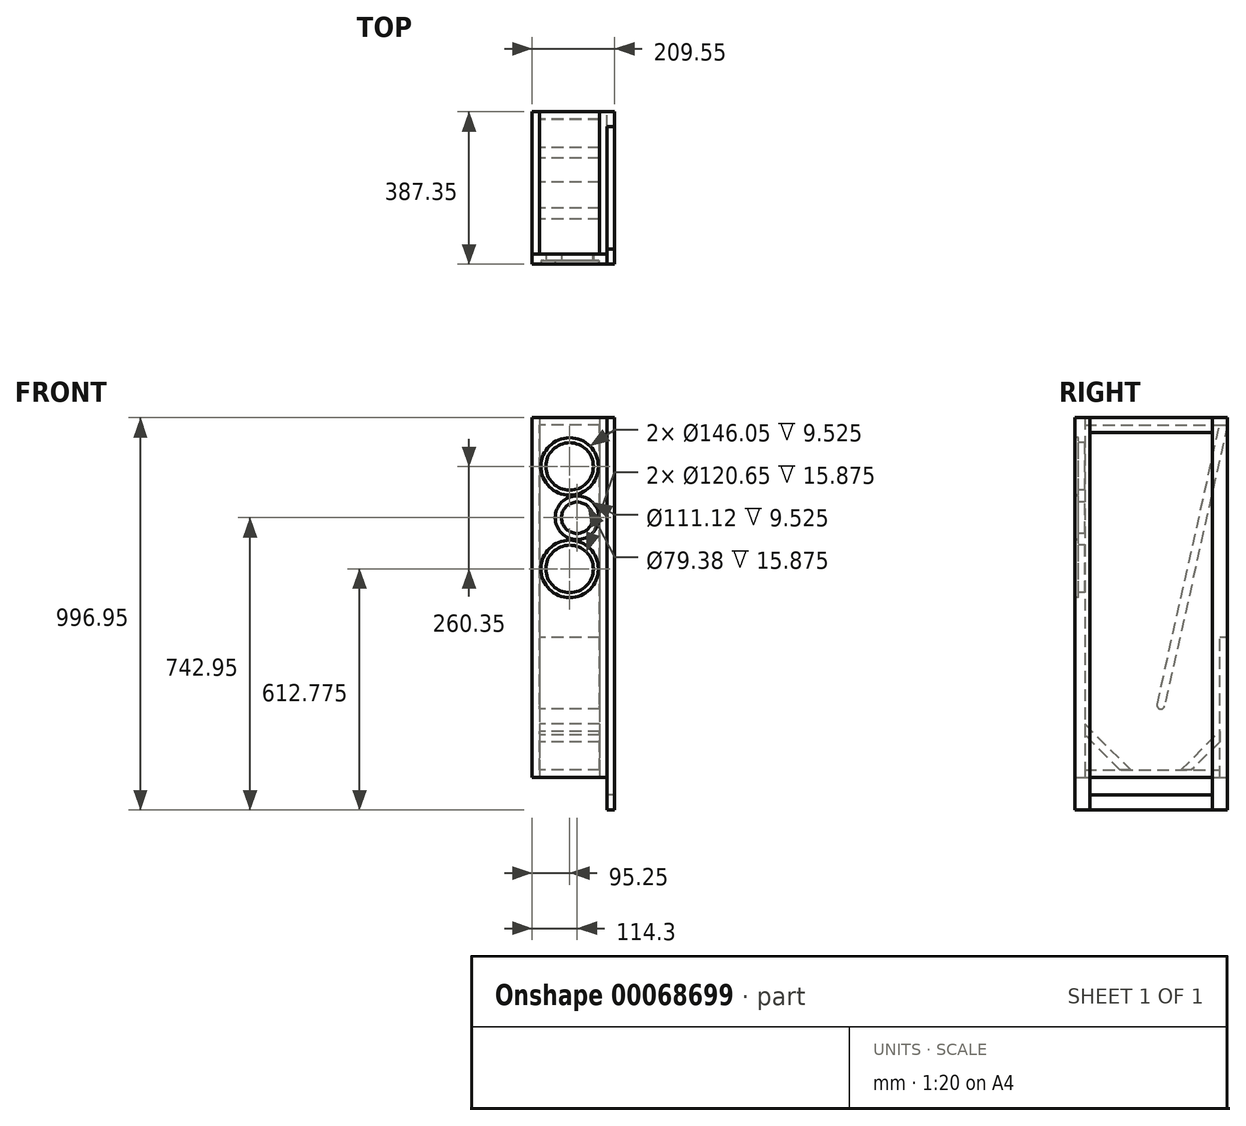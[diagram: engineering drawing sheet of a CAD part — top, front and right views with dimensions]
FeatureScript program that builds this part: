
annotation { "Feature Type Name" : "Feature", "Feature Type Description" : "" }
export const myFeature = defineFeature(function(context is Context, id is Id, definition is map)
    precondition{}
    {
        {
            var Q0;
            Q0=qCreatedBy(makeId("Front.planeOp"),FACE);
            var sketch = newSketch(context, id + "F0", { "sketchPlane" : qUnion([Q0])});
            skLineSegment(sketch, "E0.bottom", {"start": v(-95.25, 0) * mm, "end": v(95.25, 0) * mm});
            skLineSegment(sketch, "E0.top", {"start": v(-95.25, 1016) * mm, "end": v(95.25, 1016) * mm});
            skLineSegment(sketch, "E0.left", {"start": v(-95.25, 0) * mm, "end": v(-95.25, 1016) * mm});
            skLineSegment(sketch, "E0.right", {"start": v(95.25, 0) * mm, "end": v(95.25, 1016) * mm});
            skLineSegment(sketch, "E1", {"start": v(0, 0) * mm, "end": v(0, 875.2) * mm, "construction": true});
            skSolve(sketch);
        }
        {
            var Q0;
            Q0=qCreatedBy(makeId("Right.planeOp"),FACE);
            var sketch = newSketch(context, id + "F1", { "sketchPlane" : qUnion([Q0])});
            skLineSegment(sketch, "E2.bottom", {"start": v(0, 0) * mm, "end": v(361.95, 0) * mm});
            skLineSegment(sketch, "E2.top", {"start": v(0, 1016) * mm, "end": v(361.95, 1016) * mm});
            skLineSegment(sketch, "E2.left", {"start": v(0, 0) * mm, "end": v(0, 1016) * mm});
            skLineSegment(sketch, "E2.right", {"start": v(361.95, 0) * mm, "end": v(361.95, 1016) * mm});
            skSolve(sketch);
        }
        {
            var Q0;
            Q0=qCreatedBy(makeId("Front.planeOp"),FACE);
            var sketch = newSketch(context, id + "F2", { "sketchPlane" : qUnion([Q0])});
            skLineSegment(sketch, "E3.bottom", {"start": v(-95.25, 996.95) * mm, "end": v(95.25, 996.95) * mm});
            skLineSegment(sketch, "E3.top", {"start": v(-95.25, 82.55) * mm, "end": v(95.25, 82.55) * mm});
            skLineSegment(sketch, "E3.left", {"start": v(-95.25, 996.95) * mm, "end": v(-95.25, 82.55) * mm});
            skLineSegment(sketch, "E3.right", {"start": v(95.25, 996.95) * mm, "end": v(95.25, 82.55) * mm});
            skSolve(sketch);
        }
        {
            var Q0;
            Q0 = qSketchRegion(id + "F2", true);
            extrude(context, id + "F3", {"entities" : qUnion([Q0]), "depth" : 25.4 * mm});
        }
        {
            var Q0;
            Q0=makeQuery(id+"F3.opExtrude","CAP_FACE",FACE,{"disambiguationData":[OSD([sQuery(id+"F2.wireOp",EDGE,"E3.bottom"),sQuery(id+"F2.wireOp",EDGE,"E3.top"),sQuery(id+"F2.wireOp",EDGE,"E3.left"),sQuery(id+"F2.wireOp",EDGE,"E3.right")])],"isStart":false});
            var sketch = newSketch(context, id + "F4", { "sketchPlane" : qUnion([Q0])});
            skCircle(sketch, "E4", {"center": v(0, 873.12) * mm, "radius": 73.03 * mm});
            skCircle(sketch, "E5", {"center": v(19.05, 742.95) * mm, "radius": 55.56 * mm});
            skCircle(sketch, "E6", {"center": v(0, 612.77) * mm, "radius": 73.03 * mm});
            skLineSegment(sketch, "E7", {"start": v(0, 873.12) * mm, "end": v(0, 612.77) * mm, "construction": true});
            skSolve(sketch);
        }
        {
            var Q0;
            Q0 = qSketchRegion(id + "F4", true);
            extrude(context, id + "F5", {"entities" : qUnion([Q0]), "operationType" : NewBodyOperationType.REMOVE, "oppositeDirection" : true, "depth" : 9.52 * mm});
        }
        {
            var Q0;
            Q0=makeQuery(id+"F5.boolean.opBoolean","COPY",FACE,{"derivedFrom":makeQuery(id+"F5.opExtrude","CAP_FACE",FACE,{"disambiguationData":[OSD([sQuery(id+"F4.wireOp",EDGE,"E4")])],"isStart":false})});
            var sketch = newSketch(context, id + "F6", { "sketchPlane" : qUnion([Q0])});
            skCircle(sketch, "E8", {"center": v(0, 873.12) * mm, "radius": 60.33 * mm});
            skCircle(sketch, "E9", {"center": v(19.05, 742.95) * mm, "radius": 39.69 * mm});
            skCircle(sketch, "E10", {"center": v(0, 612.77) * mm, "radius": 60.33 * mm});
            skSolve(sketch);
        }
        {
            var Q0;
            Q0 = qSketchRegion(id + "F6", true);
            extrude(context, id + "F7", {"entities" : qUnion([Q0]), "operationType" : NewBodyOperationType.REMOVE, "endBound" : BoundingType.THROUGH_ALL, "oppositeDirection" : true, "depth" : 25.4 * mm});
        }
        {
            var Q0;
            Q0=makeQuery(id+"F3.opExtrude","SWEPT_FACE",FACE,{"disambiguationData":[OSD([sQuery(id+"F2.wireOp",EDGE,"E3.right")])]});
            var sketch = newSketch(context, id + "F8", { "sketchPlane" : qUnion([Q0])});
            skLineSegment(sketch, "E11.bottom", {"start": v(0, 996.95) * mm, "end": v(361.95, 996.95) * mm});
            skLineSegment(sketch, "E11.top", {"start": v(0, 82.55) * mm, "end": v(361.95, 82.55) * mm});
            skLineSegment(sketch, "E11.left", {"start": v(0, 996.95) * mm, "end": v(0, 82.55) * mm});
            skLineSegment(sketch, "E11.right", {"start": v(361.95, 996.95) * mm, "end": v(361.95, 82.55) * mm});
            skSolve(sketch);
        }
        {
            var Q0;
            Q0 = qSketchRegion(id + "F8", true);
            extrude(context, id + "F9", {"entities" : qUnion([Q0]), "oppositeDirection" : true, "depth" : 19.05 * mm});
        }
        {
            var Q0;
            Q0=makeQuery(id+"F9.opExtrude","SWEPT_BODY",BODY,{"disambiguationData":[OSD([sQuery(id+"F8.wireOp",EDGE,"E11.bottom"),sQuery(id+"F8.wireOp",EDGE,"E11.top"),sQuery(id+"F8.wireOp",EDGE,"E11.left"),sQuery(id+"F8.wireOp",EDGE,"E11.right")])]});
            var Q1;
            Q1=qCreatedBy(makeId("Right.planeOp"),FACE);
            mirror(context, id + "F10", {"entities" : qUnion([Q0]), "mirrorPlane" : qUnion([Q1])});
        }
        {
            var Q0;
            Q0=makeQuery(id+"F10.opPattern","COPY",FACE,{"derivedFrom":makeQuery(id+"F9.opExtrude","CAP_FACE",FACE,{"disambiguationData":[OSD([sQuery(id+"F8.wireOp",EDGE,"E11.bottom"),sQuery(id+"F8.wireOp",EDGE,"E11.top"),sQuery(id+"F8.wireOp",EDGE,"E11.left"),sQuery(id+"F8.wireOp",EDGE,"E11.right")])],"isStart":false}),"instanceName":"1"});
            var sketch = newSketch(context, id + "F11", { "sketchPlane" : qUnion([Q0])});
            skLineSegment(sketch, "E12.bottom", {"start": v(361.95, 82.55) * mm, "end": v(342.9, 82.55) * mm});
            skLineSegment(sketch, "E12.top", {"start": v(361.95, 438.15) * mm, "end": v(342.9, 438.15) * mm});
            skLineSegment(sketch, "E12.left", {"start": v(361.95, 82.55) * mm, "end": v(361.95, 438.15) * mm});
            skLineSegment(sketch, "E12.right", {"start": v(342.9, 82.55) * mm, "end": v(342.9, 438.15) * mm});
            skSolve(sketch);
        }
        {
            var Q0;
            Q0 = qSketchRegion(id + "F11", true);
            extrude(context, id + "F12", {"entities" : qUnion([Q0]), "depth" : 152.4 * mm});
        }
        {
            var Q0;
            Q0=makeQuery(id+"F10.opPattern","COPY",FACE,{"derivedFrom":makeQuery(id+"F9.opExtrude","CAP_FACE",FACE,{"disambiguationData":[OSD([sQuery(id+"F8.wireOp",EDGE,"E11.bottom"),sQuery(id+"F8.wireOp",EDGE,"E11.top"),sQuery(id+"F8.wireOp",EDGE,"E11.left"),sQuery(id+"F8.wireOp",EDGE,"E11.right")])],"isStart":false}),"instanceName":"1"});
            var sketch = newSketch(context, id + "F13", { "sketchPlane" : qUnion([Q0])});
            skLineSegment(sketch, "E13.bottom", {"start": v(0, 996.95) * mm, "end": v(361.95, 996.95) * mm});
            skLineSegment(sketch, "E13.top", {"start": v(0, 977.9) * mm, "end": v(361.95, 977.9) * mm});
            skLineSegment(sketch, "E13.left", {"start": v(0, 996.95) * mm, "end": v(0, 977.9) * mm});
            skLineSegment(sketch, "E13.right", {"start": v(361.95, 996.95) * mm, "end": v(361.95, 977.9) * mm});
            skSolve(sketch);
        }
        {
            var Q0;
            Q0 = qSketchRegion(id + "F13", true);
            extrude(context, id + "F14", {"entities" : qUnion([Q0]), "depth" : 152.4 * mm});
        }
        {
            var Q0;
            Q0=makeQuery(id+"F10.opPattern","COPY",FACE,{"derivedFrom":makeQuery(id+"F9.opExtrude","CAP_FACE",FACE,{"disambiguationData":[OSD([sQuery(id+"F8.wireOp",EDGE,"E11.bottom"),sQuery(id+"F8.wireOp",EDGE,"E11.top"),sQuery(id+"F8.wireOp",EDGE,"E11.left"),sQuery(id+"F8.wireOp",EDGE,"E11.right")])],"isStart":false}),"instanceName":"1"});
            var sketch = newSketch(context, id + "F15", { "sketchPlane" : qUnion([Q0])});
            skLineSegment(sketch, "E14", {"start": v(361.95, 977.9) * mm, "end": v(202.41, 264.18) * mm});
            skLineSegment(sketch, "E15", {"start": v(202.41, 264.18) * mm, "end": v(183.82, 268.34) * mm, "construction": true});
            skLineSegment(sketch, "E16", {"start": v(183.82, 268.34) * mm, "end": v(342.43, 977.9) * mm});
            skLineSegment(sketch, "E17", {"start": v(342.43, 977.9) * mm, "end": v(361.95, 977.9) * mm});
            skLineSegment(sketch, "E18", {"start": v(241.3, 438.15) * mm, "end": v(342.9, 438.15) * mm, "construction": true});
            skArc(sketch, "E19", {"start": v(183.82, 268.34) * mm, "mid": v(191.04, 256.96) * mm, "end": v(202.41, 264.18) * mm});
            skLineSegment(sketch, "E20", {"start": v(181.74, 259.04) * mm, "end": v(200.33, 254.88) * mm, "construction": true});
            skSolve(sketch);
        }
        {
            var Q0;
            Q0 = qSketchRegion(id + "F15", true);
            extrude(context, id + "F16", {"entities" : qUnion([Q0]), "depth" : 152.4 * mm});
        }
        {
            var Q0;
            Q0=makeQuery(id+"F10.opPattern","COPY",FACE,{"derivedFrom":makeQuery(id+"F9.opExtrude","CAP_FACE",FACE,{"disambiguationData":[OSD([sQuery(id+"F8.wireOp",EDGE,"E11.bottom"),sQuery(id+"F8.wireOp",EDGE,"E11.top"),sQuery(id+"F8.wireOp",EDGE,"E11.left"),sQuery(id+"F8.wireOp",EDGE,"E11.right")])],"isStart":false}),"instanceName":"1"});
            var sketch = newSketch(context, id + "F17", { "sketchPlane" : qUnion([Q0])});
            skLineSegment(sketch, "E21.bottom", {"start": v(0, 82.55) * mm, "end": v(342.9, 82.55) * mm});
            skLineSegment(sketch, "E21.top", {"start": v(0, 101.6) * mm, "end": v(342.9, 101.6) * mm});
            skLineSegment(sketch, "E21.left", {"start": v(0, 82.55) * mm, "end": v(0, 101.6) * mm});
            skLineSegment(sketch, "E21.right", {"start": v(342.9, 82.55) * mm, "end": v(342.9, 101.6) * mm});
            skSolve(sketch);
        }
        {
            var Q0;
            Q0 = qSketchRegion(id + "F17", true);
            extrude(context, id + "F18", {"entities" : qUnion([Q0]), "depth" : 152.4 * mm});
        }
        {
            var Q0;
            Q0=makeQuery(id+"F10.opPattern","COPY",FACE,{"derivedFrom":makeQuery(id+"F9.opExtrude","CAP_FACE",FACE,{"disambiguationData":[OSD([sQuery(id+"F8.wireOp",EDGE,"E11.bottom"),sQuery(id+"F8.wireOp",EDGE,"E11.top"),sQuery(id+"F8.wireOp",EDGE,"E11.left"),sQuery(id+"F8.wireOp",EDGE,"E11.right")])],"isStart":false}),"instanceName":"1"});
            var sketch = newSketch(context, id + "F19", { "sketchPlane" : qUnion([Q0])});
            skLineSegment(sketch, "E22", {"start": v(244.12, 101.6) * mm, "end": v(342.9, 200.38) * mm});
            skLineSegment(sketch, "E23", {"start": v(342.9, 200.38) * mm, "end": v(342.9, 173.44) * mm});
            skLineSegment(sketch, "E24", {"start": v(342.9, 173.44) * mm, "end": v(271.06, 101.6) * mm});
            skLineSegment(sketch, "E25", {"start": v(271.06, 101.6) * mm, "end": v(244.12, 101.6) * mm});
            skSolve(sketch);
        }
        {
            var Q0;
            Q0 = qSketchRegion(id + "F19", true);
            extrude(context, id + "F20", {"entities" : qUnion([Q0]), "depth" : 152.4 * mm});
        }
        {
            var Q0;
            Q0=makeQuery(id+"F10.opPattern","COPY",FACE,{"derivedFrom":makeQuery(id+"F9.opExtrude","CAP_FACE",FACE,{"disambiguationData":[OSD([sQuery(id+"F8.wireOp",EDGE,"E11.bottom"),sQuery(id+"F8.wireOp",EDGE,"E11.top"),sQuery(id+"F8.wireOp",EDGE,"E11.left"),sQuery(id+"F8.wireOp",EDGE,"E11.right")])],"isStart":false}),"instanceName":"1"});
            var sketch = newSketch(context, id + "F21", { "sketchPlane" : qUnion([Q0])});
            skLineSegment(sketch, "E26", {"start": v(0, 218.34) * mm, "end": v(116.74, 101.6) * mm});
            skLineSegment(sketch, "E27", {"start": v(116.74, 101.6) * mm, "end": v(89.8, 101.6) * mm});
            skLineSegment(sketch, "E28", {"start": v(89.8, 101.6) * mm, "end": v(0, 191.4) * mm});
            skLineSegment(sketch, "E29", {"start": v(0, 191.4) * mm, "end": v(0, 218.34) * mm});
            skSolve(sketch);
        }
        {
            var Q0;
            Q0 = qSketchRegion(id + "F21", true);
            extrude(context, id + "F22", {"entities" : qUnion([Q0]), "depth" : 152.4 * mm});
        }
        {
            var Q0;
            Q0=makeQuery(id+"F9.opExtrude","CAP_FACE",FACE,{"disambiguationData":[OSD([sQuery(id+"F8.wireOp",EDGE,"E11.bottom"),sQuery(id+"F8.wireOp",EDGE,"E11.top"),sQuery(id+"F8.wireOp",EDGE,"E11.left"),sQuery(id+"F8.wireOp",EDGE,"E11.right")])],"isStart":true});
            var sketch = newSketch(context, id + "F23", { "sketchPlane" : qUnion([Q0])});
            skLineSegment(sketch, "E30.bottom", {"start": v(-25.4, 0) * mm, "end": v(12.7, 0) * mm});
            skLineSegment(sketch, "E30.top", {"start": v(-25.4, 996.95) * mm, "end": v(12.7, 996.95) * mm});
            skLineSegment(sketch, "E30.left", {"start": v(-25.4, 0) * mm, "end": v(-25.4, 996.95) * mm});
            skLineSegment(sketch, "E30.right", {"start": v(12.7, 0) * mm, "end": v(12.7, 996.95) * mm});
            skSolve(sketch);
        }
        {
            var Q0;
            Q0 = qSketchRegion(id + "F23", true);
            extrude(context, id + "F24", {"entities" : qUnion([Q0]), "depth" : 19.05 * mm});
        }
        {
            var Q0;
            Q0=makeQuery(id+"F9.opExtrude","CAP_FACE",FACE,{"disambiguationData":[OSD([sQuery(id+"F8.wireOp",EDGE,"E11.bottom"),sQuery(id+"F8.wireOp",EDGE,"E11.top"),sQuery(id+"F8.wireOp",EDGE,"E11.left"),sQuery(id+"F8.wireOp",EDGE,"E11.right")])],"isStart":true});
            var sketch = newSketch(context, id + "F25", { "sketchPlane" : qUnion([Q0])});
            skLineSegment(sketch, "E31.bottom", {"start": v(361.95, 996.95) * mm, "end": v(323.85, 996.95) * mm});
            skLineSegment(sketch, "E31.top", {"start": v(361.95, 0) * mm, "end": v(323.85, 0) * mm});
            skLineSegment(sketch, "E31.left", {"start": v(361.95, 996.95) * mm, "end": v(361.95, 0) * mm});
            skLineSegment(sketch, "E31.right", {"start": v(323.85, 996.95) * mm, "end": v(323.85, 0) * mm});
            skSolve(sketch);
        }
        {
            var Q0;
            Q0 = qSketchRegion(id + "F25", true);
            extrude(context, id + "F26", {"entities" : qUnion([Q0]), "operationType" : NewBodyOperationType.ADD, "depth" : 19.05 * mm});
        }
        {
            var Q0;
            Q0=makeQuery(id+"F9.opExtrude","CAP_FACE",FACE,{"disambiguationData":[OSD([sQuery(id+"F8.wireOp",EDGE,"E11.bottom"),sQuery(id+"F8.wireOp",EDGE,"E11.top"),sQuery(id+"F8.wireOp",EDGE,"E11.left"),sQuery(id+"F8.wireOp",EDGE,"E11.right")])],"isStart":true});
            var sketch = newSketch(context, id + "F27", { "sketchPlane" : qUnion([Q0])});
            skLineSegment(sketch, "E32.bottom", {"start": v(12.7, 996.95) * mm, "end": v(323.85, 996.95) * mm});
            skLineSegment(sketch, "E32.top", {"start": v(12.7, 958.85) * mm, "end": v(323.85, 958.85) * mm});
            skLineSegment(sketch, "E32.left", {"start": v(12.7, 996.95) * mm, "end": v(12.7, 958.85) * mm});
            skLineSegment(sketch, "E32.right", {"start": v(323.85, 996.95) * mm, "end": v(323.85, 958.85) * mm});
            skSolve(sketch);
        }
        {
            var Q0;
            Q0 = qSketchRegion(id + "F27", true);
            extrude(context, id + "F28", {"entities" : qUnion([Q0]), "depth" : 19.05 * mm});
        }
        {
            var Q0;
            Q0=makeQuery(id+"F9.opExtrude","CAP_FACE",FACE,{"disambiguationData":[OSD([sQuery(id+"F8.wireOp",EDGE,"E11.bottom"),sQuery(id+"F8.wireOp",EDGE,"E11.top"),sQuery(id+"F8.wireOp",EDGE,"E11.left"),sQuery(id+"F8.wireOp",EDGE,"E11.right")])],"isStart":true});
            var sketch = newSketch(context, id + "F29", { "sketchPlane" : qUnion([Q0])});
            skLineSegment(sketch, "E33.bottom", {"start": v(12.7, 0) * mm, "end": v(323.85, 0) * mm});
            skLineSegment(sketch, "E33.top", {"start": v(12.7, 38.1) * mm, "end": v(323.85, 38.1) * mm});
            skLineSegment(sketch, "E33.left", {"start": v(12.7, 0) * mm, "end": v(12.7, 38.1) * mm});
            skLineSegment(sketch, "E33.right", {"start": v(323.85, 0) * mm, "end": v(323.85, 38.1) * mm});
            skSolve(sketch);
        }
        {
            var Q0;
            Q0 = qSketchRegion(id + "F29", true);
            extrude(context, id + "F30", {"entities" : qUnion([Q0]), "depth" : 19.05 * mm});
        }
    });
